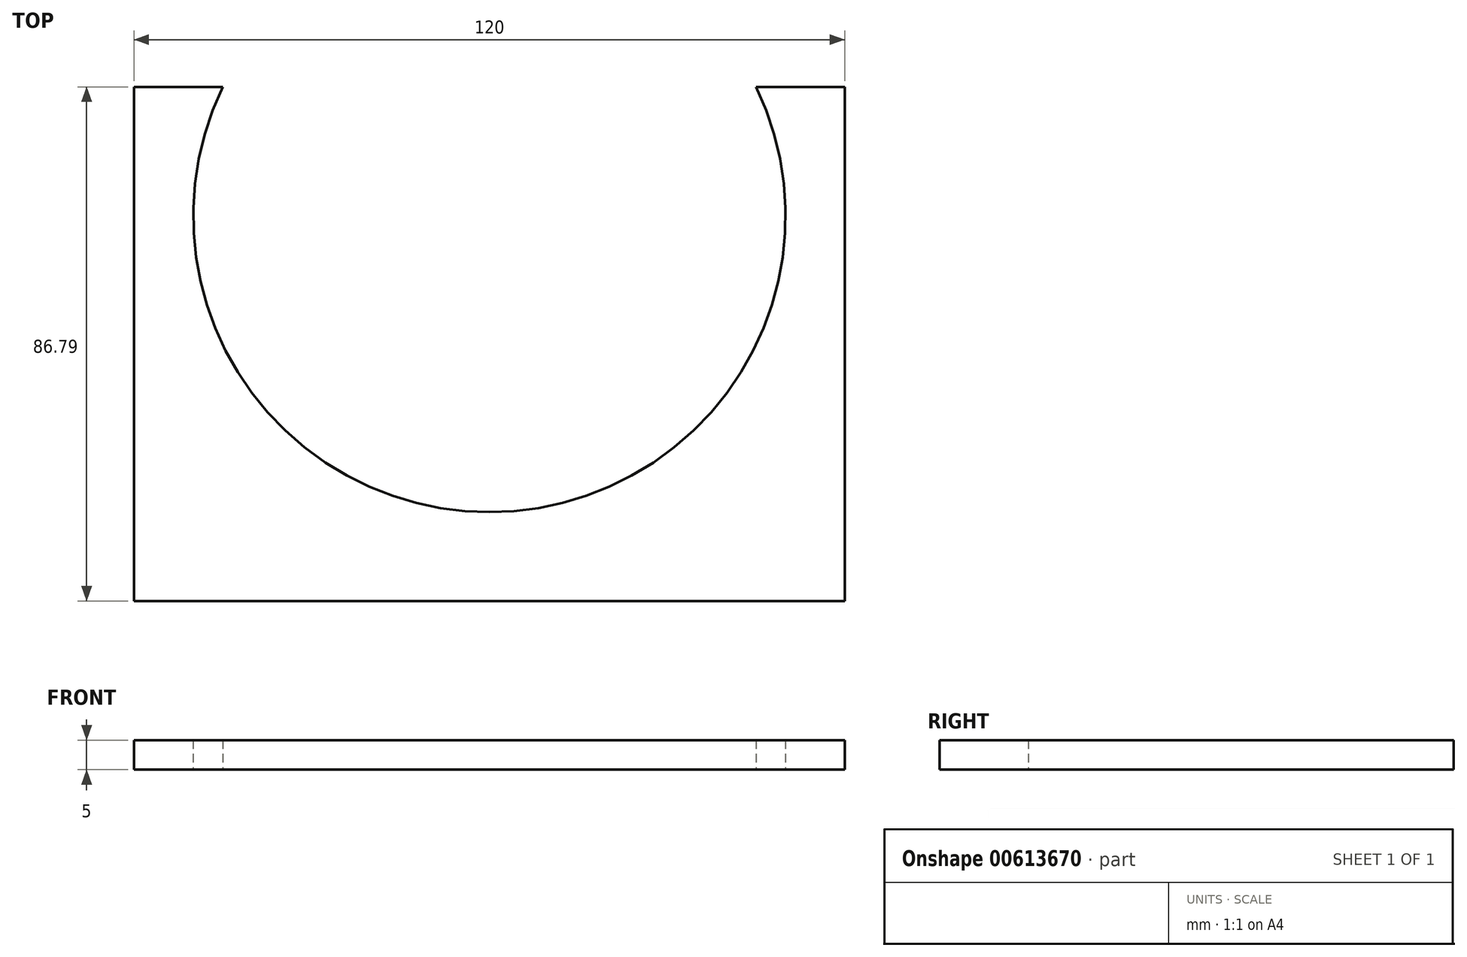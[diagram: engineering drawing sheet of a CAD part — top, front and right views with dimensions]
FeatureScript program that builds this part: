
annotation { "Feature Type Name" : "Feature", "Feature Type Description" : "" }
export const myFeature = defineFeature(function(context is Context, id is Id, definition is map)
    precondition{}
    {
        {
            var Q0;
            Q0=qCreatedBy(makeId("Top.planeOp"),FACE);
            var sketch = newSketch(context, id + "F0", { "sketchPlane" : qUnion([Q0])});
            skArc(sketch, "E0", {"start": v(-45, 21.8) * mm, "mid": v(0, -50) * mm, "end": v(45, 21.8) * mm});
            skLineSegment(sketch, "E1.top", {"start": v(-60, -65) * mm, "end": v(0, -65) * mm});
            skLineSegment(sketch, "E1.right", {"start": v(60, 21.8) * mm, "end": v(60, -65) * mm});
            skLineSegment(sketch, "E2", {"start": v(-60, 21.8) * mm, "end": v(-45, 21.8) * mm});
            skLineSegment(sketch, "E3", {"start": v(60, 21.8) * mm, "end": v(45, 21.8) * mm});
            skLineSegment(sketch, "E4.0", {"start": v(-60, 21.8) * mm, "end": v(-60, -65) * mm});
            skLineSegment(sketch, "E5", {"start": v(0, -65) * mm, "end": v(60, -65) * mm});
            skSolve(sketch);
        }
        {
            var Q0;
            Q0 = qSketchRegion(id + "F0", true);
            extrude(context, id + "F1", {"entities" : qUnion([Q0]), "depth" : 5 * mm, "offsetDistance" : 25 * mm});
        }
    });
